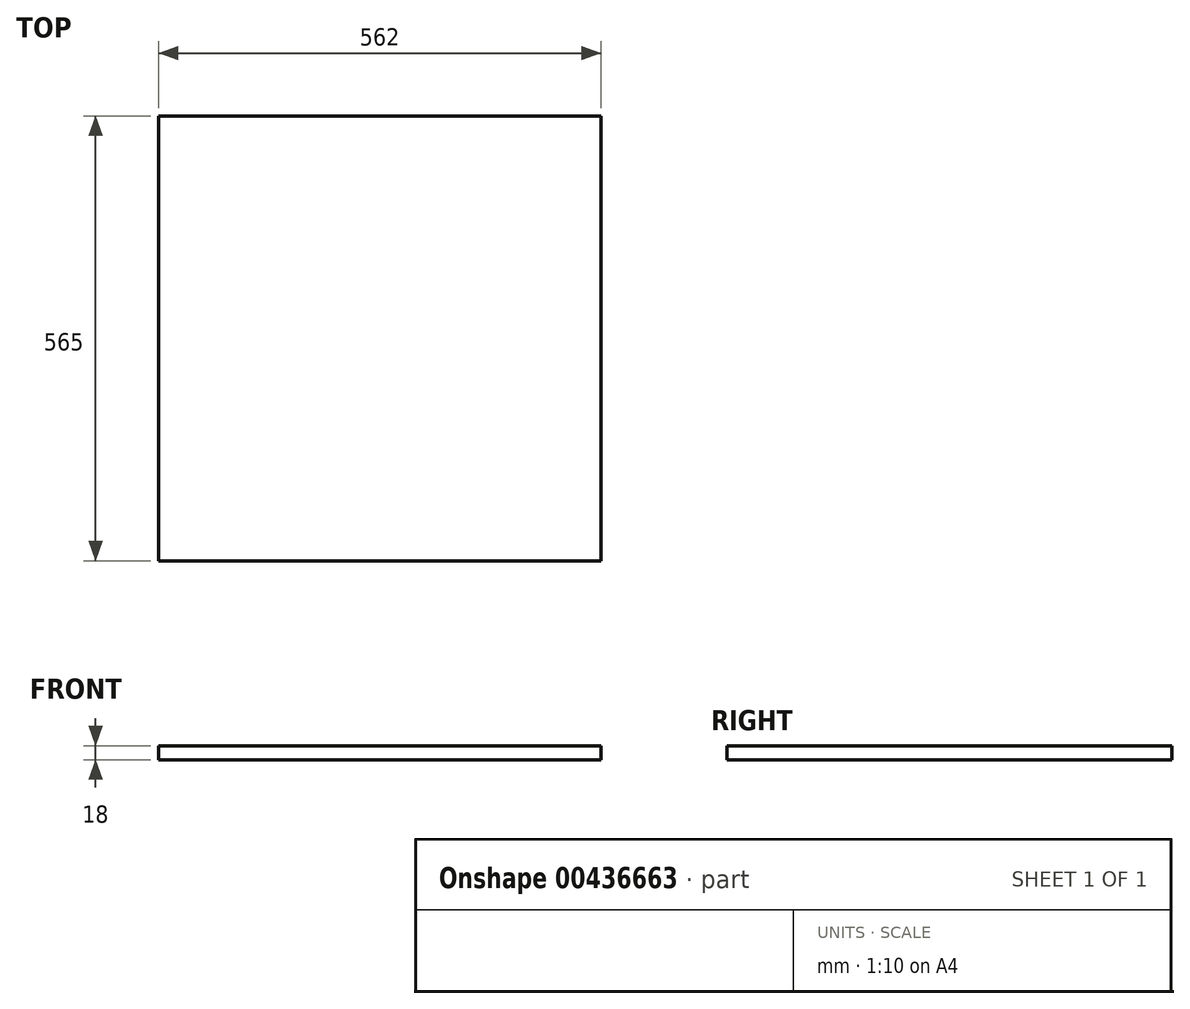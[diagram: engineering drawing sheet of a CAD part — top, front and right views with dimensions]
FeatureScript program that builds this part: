
annotation { "Feature Type Name" : "Feature", "Feature Type Description" : "" }
export const myFeature = defineFeature(function(context is Context, id is Id, definition is map)
    precondition{}
    {
        {
            var Q0;
            Q0=qCreatedBy(makeId("Top.planeOp"),FACE);
            var sketch = newSketch(context, id + "F0", { "sketchPlane" : qUnion([Q0])});
            skLineSegment(sketch, "E0.bottom", {"start": v(281, 282.5) * mm, "end": v(-281, 282.5) * mm});
            skLineSegment(sketch, "E0.top", {"start": v(281, -282.5) * mm, "end": v(-281, -282.5) * mm});
            skLineSegment(sketch, "E0.left", {"start": v(281, 282.5) * mm, "end": v(281, -282.5) * mm});
            skLineSegment(sketch, "E0.right", {"start": v(-281, 282.5) * mm, "end": v(-281, -282.5) * mm});
            skPoint(sketch, "E0.middle", {"position": v(0, 0) * mm});
            skSolve(sketch);
        }
        {
            var Q0;
            Q0=makeQuery(id+"F0.imprint","IMPRINT",FACE,{"disambiguationData":[TD([[makeQuery(id+"F0.imprint","IMPRINT",EDGE,{"derivedFrom":sQuery(id+"F0.wireOp",EDGE,"E0.bottom")}),1.0]])]});
            extrude(context, id + "F1", {"entities" : qUnion([Q0]), "depth" : 18 * mm});
        }
    });
